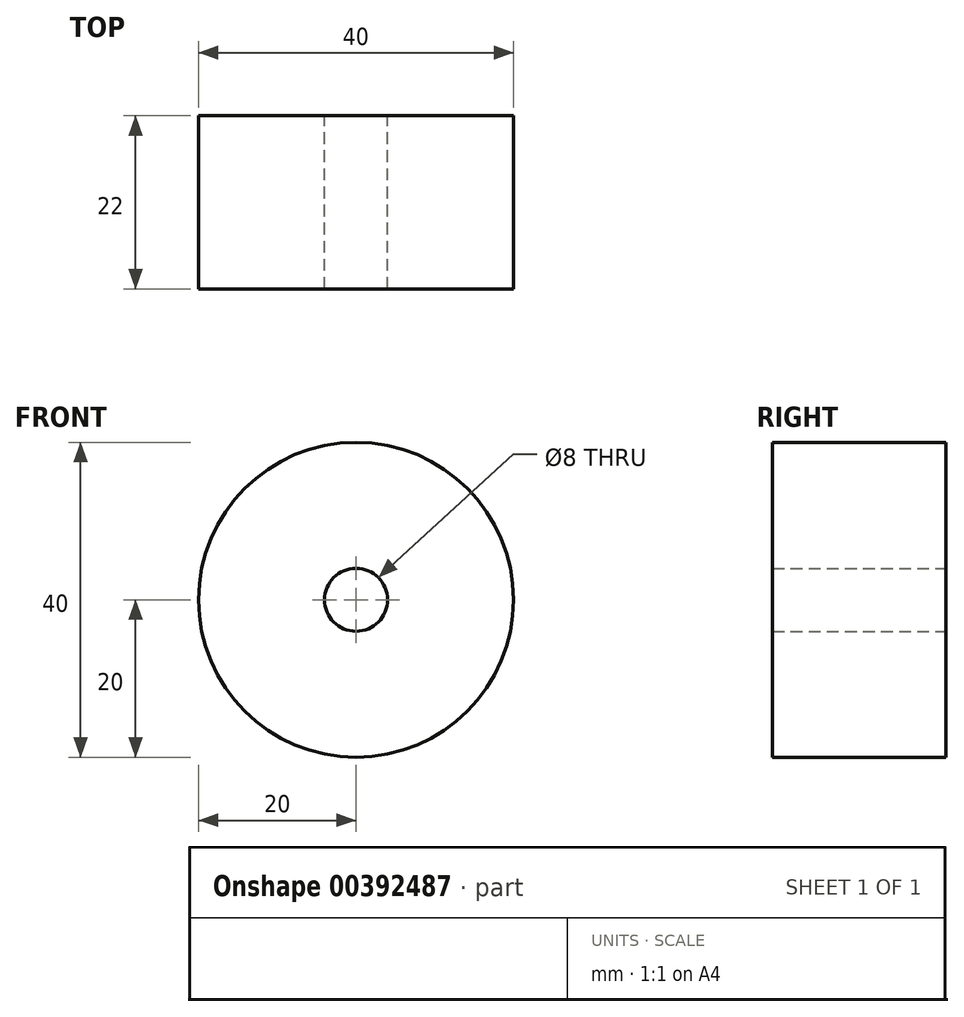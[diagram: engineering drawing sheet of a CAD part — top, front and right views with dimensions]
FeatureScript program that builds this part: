
annotation { "Feature Type Name" : "Feature", "Feature Type Description" : "" }
export const myFeature = defineFeature(function(context is Context, id is Id, definition is map)
    precondition{}
    {
        {
            var Q0;
            Q0=qCreatedBy(makeId("Front.planeOp"), FACE);
            var sketch = newSketch(context, id + "F0", { "sketchPlane" : qUnion([Q0])});
            skCircle(sketch, "E0", {"center": v(0, 0) * mm, "radius": 4 * mm});
            skCircle(sketch, "E1", {"center": v(0, 0) * mm, "radius": 20 * mm});
            skSolve(sketch);
        }
        {
            var Q0;
            Q0 = qSketchRegion(id + "F0", true);
            extrude(context, id + "F1", {"entities" : qUnion([Q0]), "depth" : 22 * mm, "offsetDistance" : 25 * mm});
        }
    });
